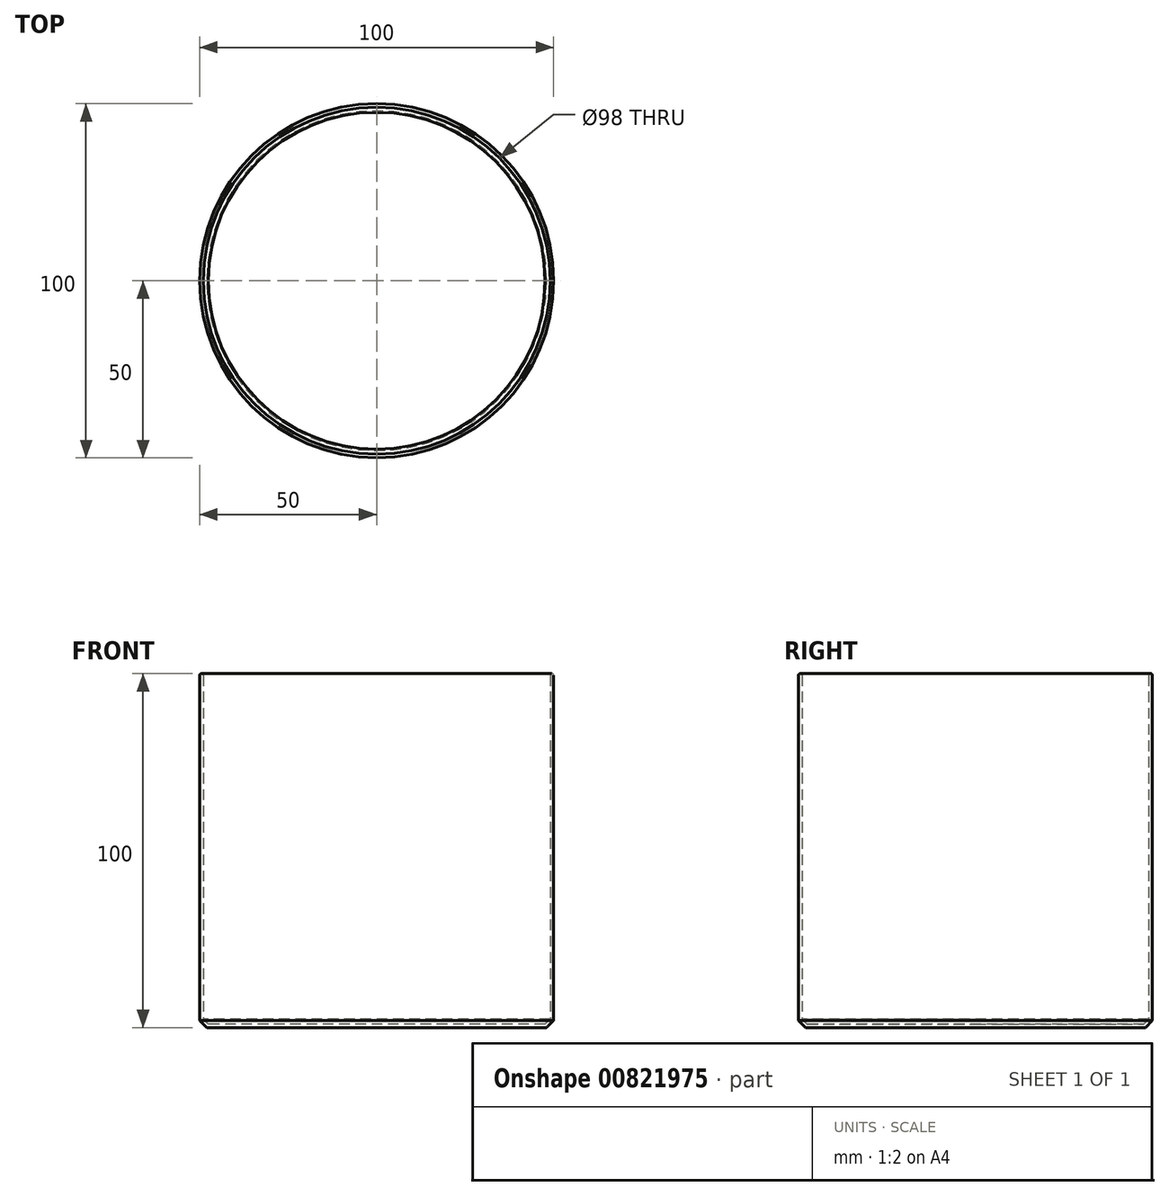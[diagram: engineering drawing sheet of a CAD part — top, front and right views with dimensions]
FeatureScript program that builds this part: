
annotation { "Feature Type Name" : "Feature", "Feature Type Description" : "" }
export const myFeature = defineFeature(function(context is Context, id is Id, definition is map)
    precondition{}
    {
        {
            var Q0;
            Q0=qCreatedBy(makeId("Top.planeOp"),FACE);
            var sketch = newSketch(context, id + "F0", { "sketchPlane" : qUnion([Q0])});
            skCircle(sketch, "E0", {"center": v(0, 0) * mm, "radius": 50 * mm});
            skSolve(sketch);
        }
        {
            var Q0;
            Q0=makeQuery(id+"F0.imprint","IMPRINT",FACE,{"disambiguationData":[TD([[makeQuery(id+"F0.imprint","IMPRINT",EDGE,{"derivedFrom":sQuery(id+"F0.wireOp",EDGE,"E0")}),1.0]])]});
            extrude(context, id + "F1", {"entities" : qUnion([Q0]), "depth" : 50 * mm, "offsetDistance" : 25 * mm});
        }
        {
            var Q0;
            Q0=makeQuery(id+"F1.opExtrude","CAP_FACE",FACE,{"disambiguationData":[OSD([sQuery(id+"F0.wireOp",EDGE,"E0")])],"isStart":true});
            extrude(context, id + "F2", {"entities" : qUnion([Q0]), "operationType" : NewBodyOperationType.ADD, "depth" : 50 * mm, "offsetDistance" : 25 * mm});
        }
        {
            var Q0;
            Q0=makeQuery(id+"F2.opExtrude","CAP_EDGE",EDGE,{"disambiguationData":[OSD([sQuery(id+"F0.wireOp",EDGE,"E0")])],"isStart":false});
            chamfer(context, id + "F3", {"entities" : qUnion([Q0]), "width" : 2 * mm, "tangentPropagation" : true});
        }
        {
            var Q0;
            Q0=makeQuery(id+"F1.opExtrude","CAP_FACE",FACE,{"disambiguationData":[OSD([sQuery(id+"F0.wireOp",EDGE,"E0")])],"isStart":false});
            shell(context, id + "F4", {"entities" : qUnion([Q0]), "thickness" : 1 * mm});
        }
        {
            var Q0;
            Q0=makeQuery(id+"F1.opExtrude","CAP_EDGE",EDGE,{"disambiguationData":[OSD([sQuery(id+"F0.wireOp",EDGE,"E0")])],"isStart":false});
            var Q1;
            {var subQ0=sQuery(id+"F0.wireOp",EDGE,"E0");Q1=makeQuery(id+"F4.opShell","OFFSET_EDGE",EDGE,{"disambiguationData":[OSD([subQ0]),TDD([makeQuery(id+"F1.opExtrude","CAP_EDGE",EDGE,{"disambiguationData":[OSD([subQ0])],"isStart":false})])]});}
            fillet(context, id + "F5", {"entities" : qUnion([Q0, Q1]), "radius" : 0.5 * mm, "tangentPropagation" : true, "allowEdgeOverflow" : false});
        }
    });
